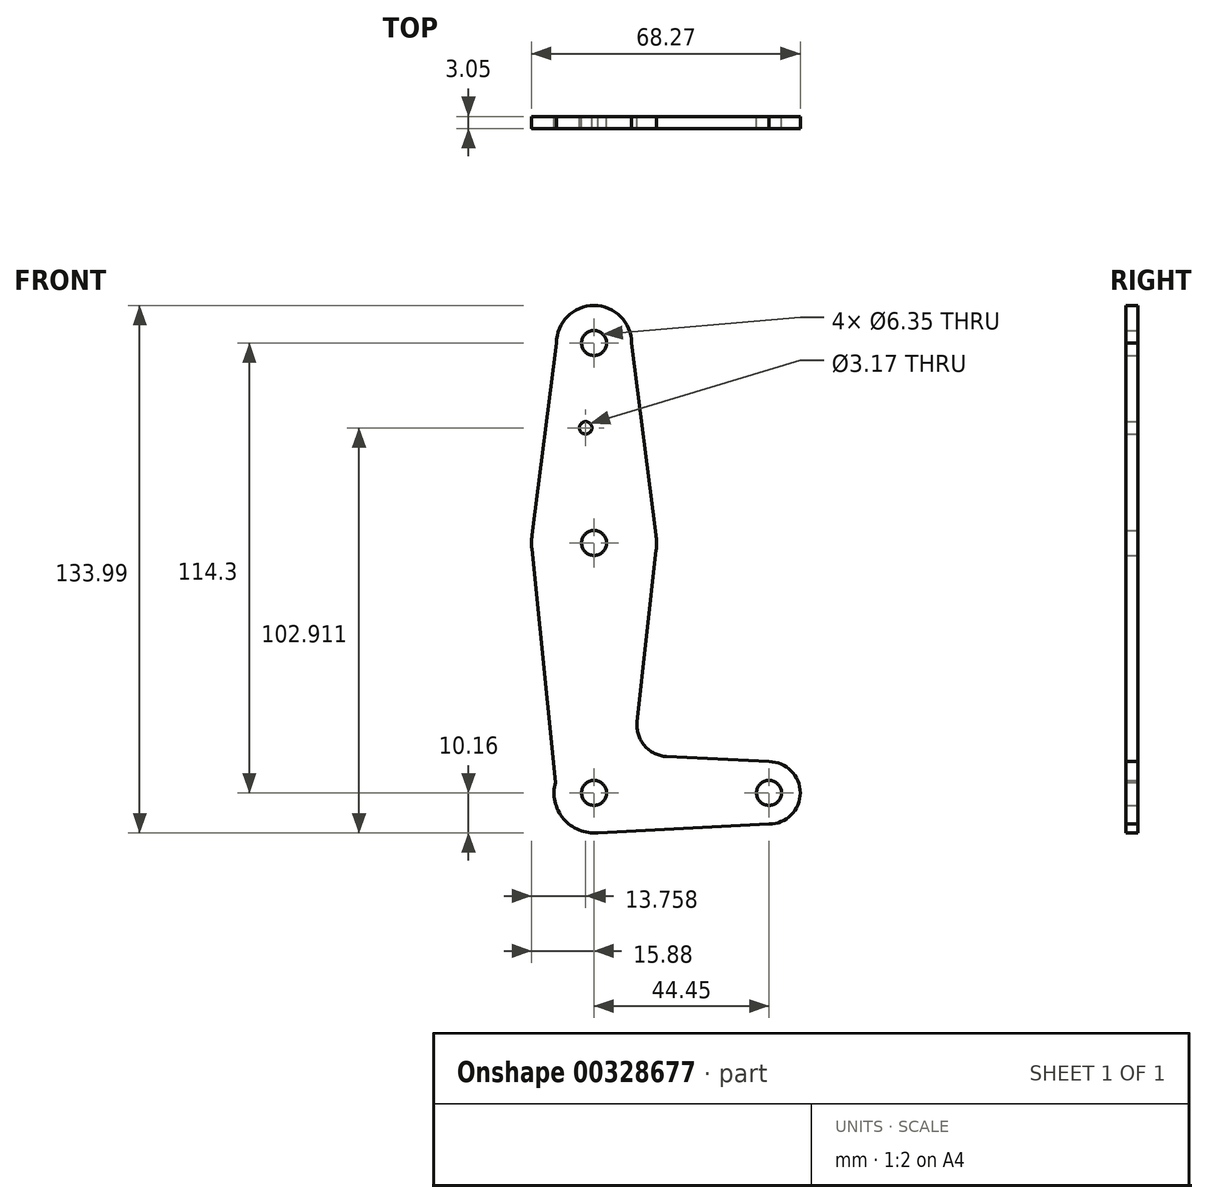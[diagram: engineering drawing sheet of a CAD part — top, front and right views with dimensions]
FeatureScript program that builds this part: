
annotation { "Feature Type Name" : "Feature", "Feature Type Description" : "" }
export const myFeature = defineFeature(function(context is Context, id is Id, definition is map)
    precondition{}
    {
        {
            var Q0;
            Q0=qCreatedBy(makeId("Front.planeOp"),FACE);
            var sketch = newSketch(context, id + "F0", { "sketchPlane" : qUnion([Q0])});
            skLineSegment(sketch, "E0", {"start": v(0, 0) * mm, "end": v(0, 114.3) * mm, "construction": true});
            skLineSegment(sketch, "E1", {"start": v(0, 0) * mm, "end": v(44.45, 0) * mm, "construction": true});
            skCircle(sketch, "E2", {"center": v(0, 114.3) * mm, "radius": 9.53 * mm});
            skCircle(sketch, "E3", {"center": v(0, 63.5) * mm, "radius": 15.88 * mm});
            skCircle(sketch, "E4", {"center": v(0, 0) * mm, "radius": 10.16 * mm});
            skCircle(sketch, "E5", {"center": v(44.45, 0) * mm, "radius": 7.94 * mm});
            skLineSegment(sketch, "E6", {"start": v(-9.53, 114.3) * mm, "end": v(-15.75, 65.5) * mm});
            skLineSegment(sketch, "E7", {"start": v(9.53, 114.3) * mm, "end": v(15.75, 65.5) * mm});
            skLineSegment(sketch, "E8", {"start": v(-15.8, 61.9) * mm, "end": v(-9.8, 2.67) * mm});
            skLineSegment(sketch, "E9", {"start": v(15.78, 61.75) * mm, "end": v(10.94, 18.05) * mm});
            skLineSegment(sketch, "E10", {"start": v(0, -10.16) * mm, "end": v(44.45, -7.94) * mm});
            skLineSegment(sketch, "E11", {"start": v(18.45, 9.24) * mm, "end": v(44.45, 7.94) * mm});
            skCircle(sketch, "E12", {"center": v(0, 114.3) * mm, "radius": 3.18 * mm});
            skCircle(sketch, "E13", {"center": v(0, 63.5) * mm, "radius": 3.18 * mm});
            skCircle(sketch, "E14", {"center": v(0, 0) * mm, "radius": 3.18 * mm});
            skCircle(sketch, "E15", {"center": v(44.45, 0) * mm, "radius": 3.18 * mm});
            skArc(sketch, "E16.filletArc", {"start": v(10.94, 18.05) * mm, "mid": v(12.8, 12.02) * mm, "end": v(18.45, 9.24) * mm});
            skCircle(sketch, "E17", {"center": v(-2.12, 92.75) * mm, "radius": 1.59 * mm});
            skSolve(sketch);
        }
        {
            var Q0;
            Q0 = qSketchRegion(id + "F0", true);
            extrude(context, id + "F1", {"entities" : qUnion([Q0]), "depth" : 3.05 * mm});
        }
    });
